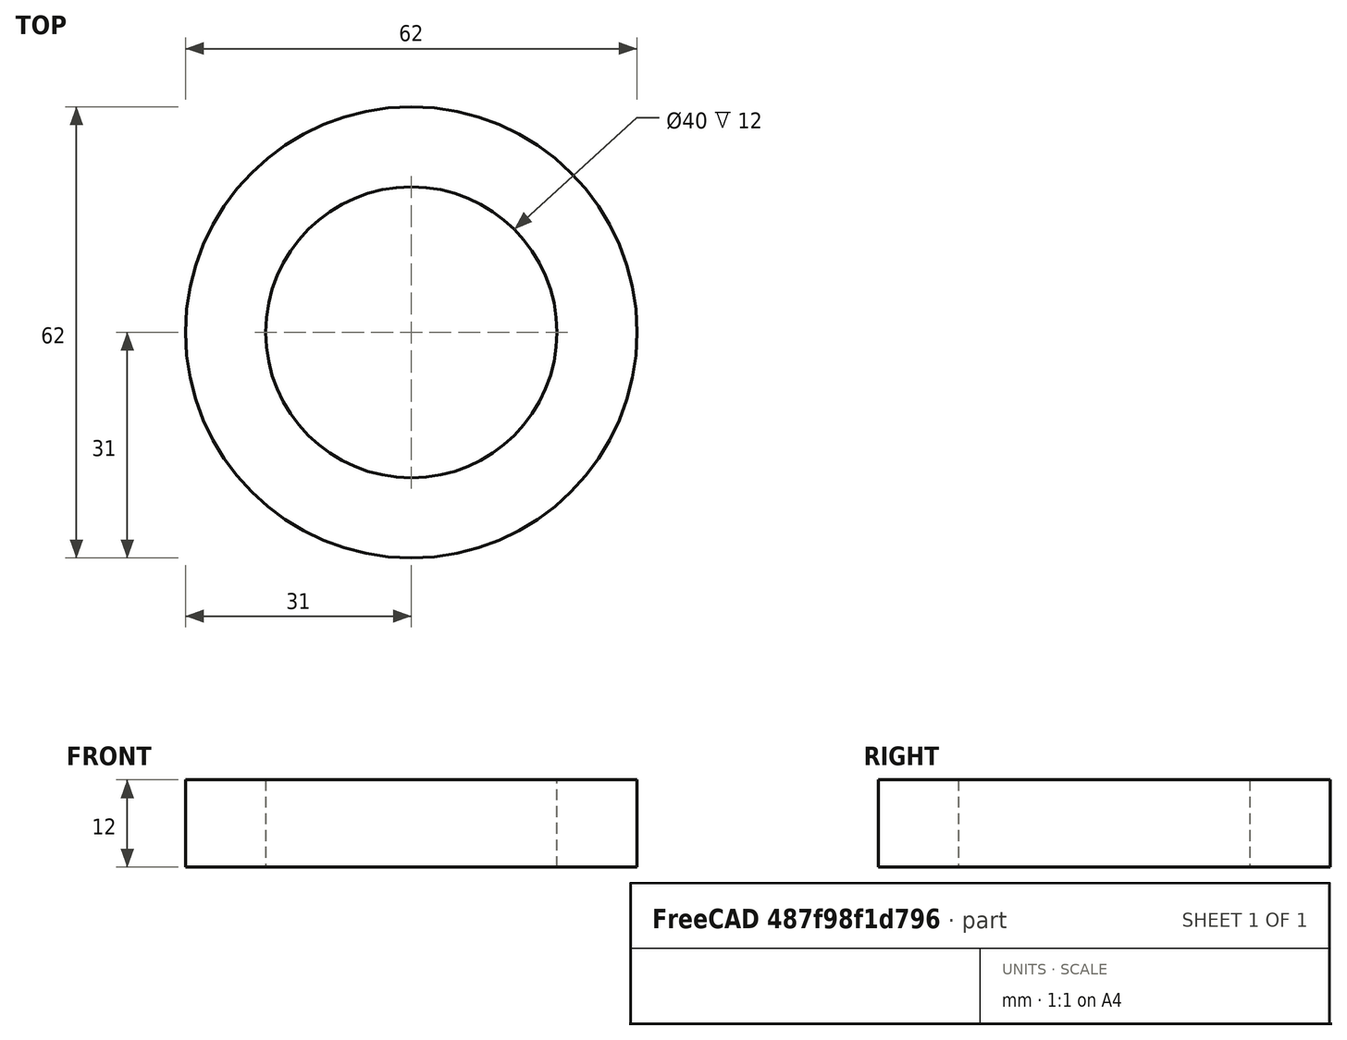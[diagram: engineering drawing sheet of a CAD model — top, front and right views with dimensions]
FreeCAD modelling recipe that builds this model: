
FCSTD DOCUMENT  (FreeCAD 0.17R13541 (Git))
Label: HP600_wheel-rubber
License: All rights reserved
LicenseURL: http://en.wikipedia.org/wiki/All_rights_reserved
objects: Sketcher::SketchObject×1, PartDesign::Pad×1, PartDesign::Body×1
note: 4 computed .brp shape members not serialized (recipe doc carries the construction recipe); baked Part::Feature solids carry a one-line shape summary decoded from their .brp

FEATURE [Sketcher::SketchObject] Sketch
  MapMode = 5
  Support = -> [XY_Plane]
  sketch-geometry (2):
    g0: Circle CenterX=0 CenterY=0 CenterZ=0 NormalX=0 NormalY=0 NormalZ=1 AngleXU=0 Radius=20
    g1: Circle CenterX=0 CenterY=0 CenterZ=0 NormalX=0 NormalY=0 NormalZ=1 AngleXU=0 Radius=31
  constraints (4):
    c: Coincident(g0,g-1)
    c: Coincident(g1,g-1)
    c: Radius(g0) = 20
    c: Radius(g1) = 31
FEATURE [PartDesign::Pad] Pad
  Length = 12
  Length2 = 100
  Midplane = true
  Profile = -> Sketch
  Type = 0
FEATURE [PartDesign::Body] Body
  Group = -> [Sketch,Pad]
  Origin = -> Origin
  Tip = -> Pad
